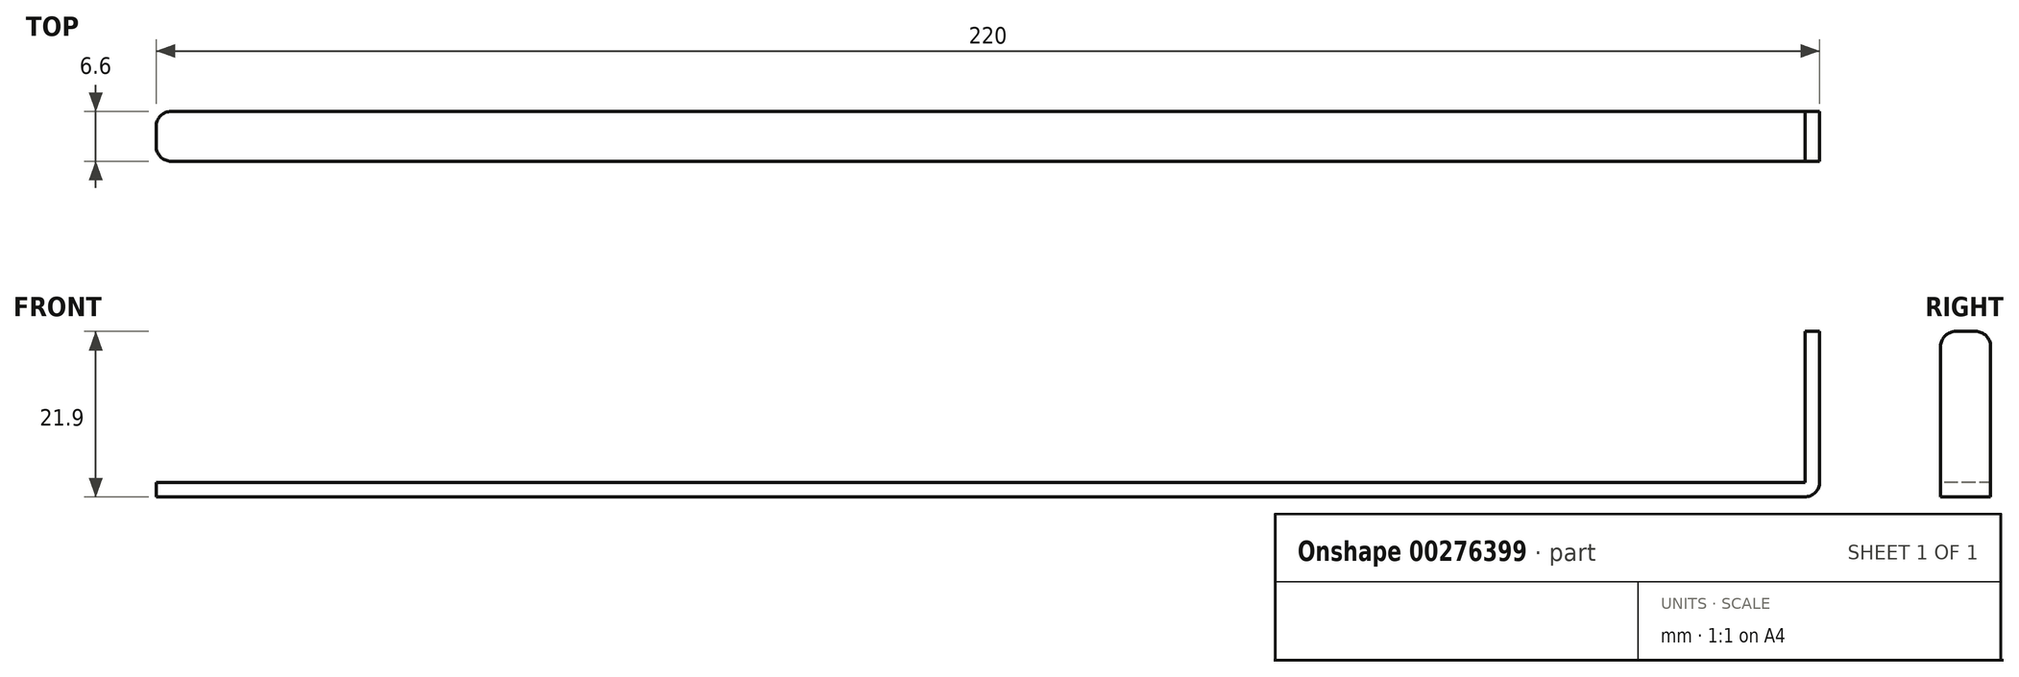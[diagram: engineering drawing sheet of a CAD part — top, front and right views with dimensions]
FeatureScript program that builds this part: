
annotation { "Feature Type Name" : "Feature", "Feature Type Description" : "" }
export const myFeature = defineFeature(function(context is Context, id is Id, definition is map)
    precondition{}
    {
        {
            var Q0;
            Q0=qCreatedBy(makeId("Top.planeOp"),FACE);
            var sketch = newSketch(context, id + "F0", { "sketchPlane" : qUnion([Q0])});
            skLineSegment(sketch, "E0.bottom", {"start": v(0, 0) * mm, "end": v(220, 0) * mm});
            skLineSegment(sketch, "E0.top", {"start": v(0, -6.6) * mm, "end": v(220, -6.6) * mm});
            skLineSegment(sketch, "E0.left", {"start": v(0, 0) * mm, "end": v(0, -6.6) * mm});
            skLineSegment(sketch, "E0.right", {"start": v(220, 0) * mm, "end": v(220, -6.6) * mm});
            skSolve(sketch);
        }
        {
            var Q0;
            Q0 = qSketchRegion(id + "F0", true);
            extrude(context, id + "F1", {"entities" : qUnion([Q0]), "depth" : 1.9 * mm, "offsetDistance" : 25 * mm});
        }
        {
            var Q0;
            Q0=makeQuery(id+"F1.opExtrude","CAP_FACE",FACE,{"disambiguationData":[OSD([sQuery(id+"F0.wireOp",EDGE,"E0.bottom"),sQuery(id+"F0.wireOp",EDGE,"E0.top"),sQuery(id+"F0.wireOp",EDGE,"E0.left"),sQuery(id+"F0.wireOp",EDGE,"E0.right")])],"isStart":false});
            var sketch = newSketch(context, id + "F2", { "sketchPlane" : qUnion([Q0])});
            skLineSegment(sketch, "E1.bottom", {"start": v(218.1, 0) * mm, "end": v(220, 0) * mm});
            skLineSegment(sketch, "E1.top", {"start": v(218.1, -6.6) * mm, "end": v(220, -6.6) * mm});
            skLineSegment(sketch, "E1.left", {"start": v(218.1, 0) * mm, "end": v(218.1, -6.6) * mm});
            skLineSegment(sketch, "E1.right", {"start": v(220, 0) * mm, "end": v(220, -6.6) * mm});
            skSolve(sketch);
        }
        {
            var Q0;
            Q0 = qSketchRegion(id + "F2", true);
            extrude(context, id + "F3", {"entities" : qUnion([Q0]), "operationType" : NewBodyOperationType.ADD, "depth" : 20 * mm, "offsetDistance" : 25 * mm});
        }
        {
            var Q0;
            Q0=makeQuery(id+"F1.opExtrude","CAP_EDGE",EDGE,{"disambiguationData":[OSD([sQuery(id+"F0.wireOp",EDGE,"E0.right")])],"isStart":true});
            var Q1;
            Q1=makeQuery(id+"F3.opExtrude","CAP_EDGE",EDGE,{"disambiguationData":[OSD([sQuery(id+"F2.wireOp",EDGE,"E1.left")])],"isStart":true});
            var Q2;
            Q2=makeQuery(id+"F3.opExtrude","CAP_EDGE",EDGE,{"disambiguationData":[OSD([sQuery(id+"F2.wireOp",EDGE,"E1.top")])],"isStart":false});
            var Q3;
            Q3=makeQuery(id+"F3.opExtrude","CAP_EDGE",EDGE,{"disambiguationData":[OSD([sQuery(id+"F2.wireOp",EDGE,"E1.bottom")])],"isStart":false});
            var Q4;
            Q4=makeQuery(id+"F1.opExtrude","SWEPT_EDGE",EDGE,{"disambiguationData":[OSD([sQuery(id+"F0.wireOp",EDGE,"E0.top"),sQuery(id+"F0.wireOp",EDGE,"E0.left")])]});
            var Q5;
            Q5=makeQuery(id+"F1.opExtrude","SWEPT_EDGE",EDGE,{"disambiguationData":[OSD([sQuery(id+"F0.wireOp",EDGE,"E0.bottom"),sQuery(id+"F0.wireOp",EDGE,"E0.left")])]});
            fillet(context, id + "F4", {"entities" : qUnion([Q0, Q1, Q2, Q3, Q4, Q5]), "tangentPropagation" : true, "radius" : 2 * mm, "defaultsChanged" : false, "vertexSettings" : [], "allowEdgeOverflow" : false});
        }
    });
